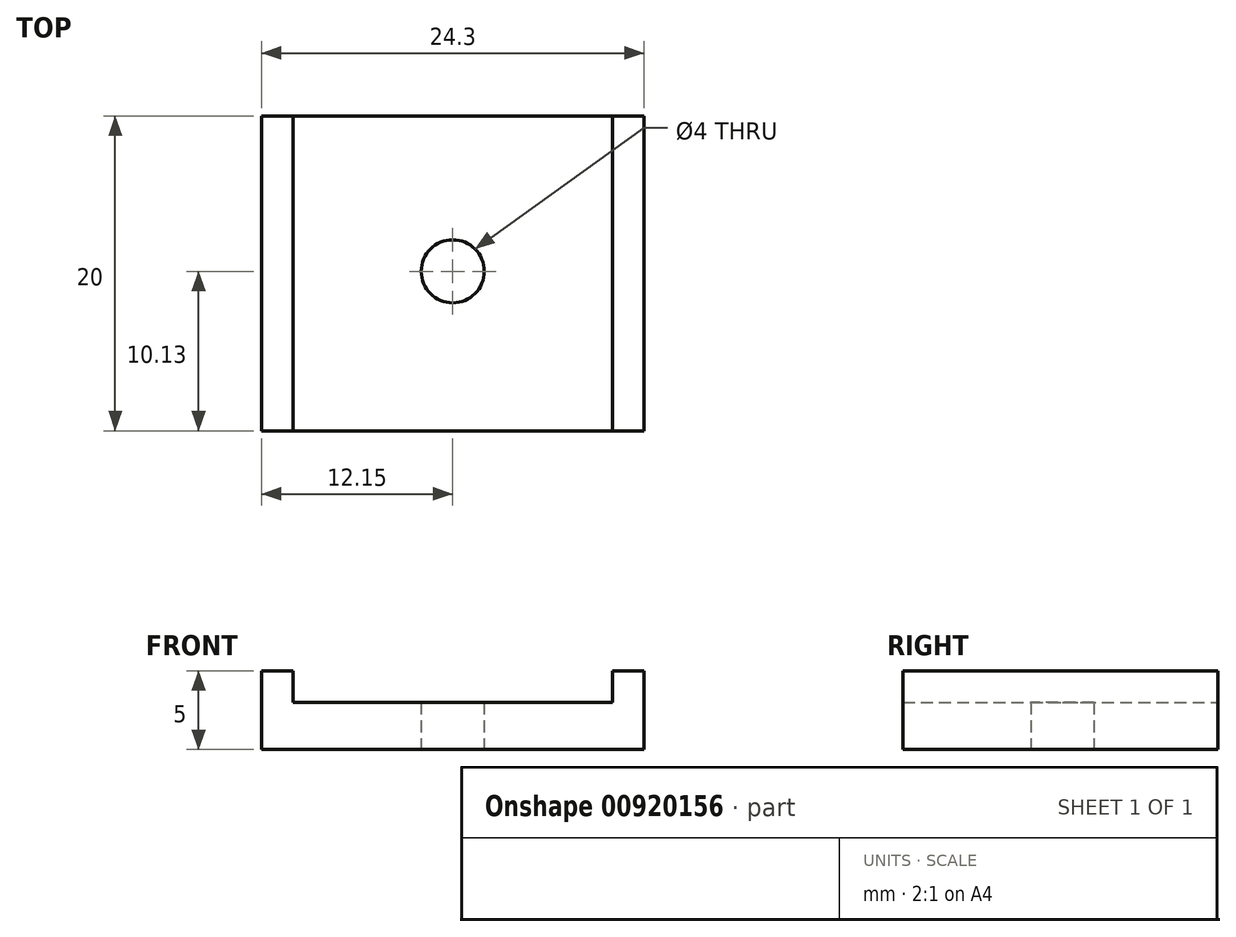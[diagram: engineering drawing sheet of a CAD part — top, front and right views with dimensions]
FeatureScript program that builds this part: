
annotation { "Feature Type Name" : "Feature", "Feature Type Description" : "" }
export const myFeature = defineFeature(function(context is Context, id is Id, definition is map)
    precondition{}
    {
        {
            var Q0;
            Q0=qCreatedBy(makeId("Top.planeOp"),FACE);
            var sketch = newSketch(context, id + "F0", { "sketchPlane" : qUnion([Q0])});
            skLineSegment(sketch, "E0", {"start": v(0, 0) * mm, "end": v(0, 41.66) * mm, "construction": true});
            skLineSegment(sketch, "E1", {"start": v(0, -0.13) * mm, "end": v(10.15, -0.13) * mm});
            skLineSegment(sketch, "E2", {"start": v(10.15, 19.87) * mm, "end": v(0, 19.87) * mm});
            skLineSegment(sketch, "E3.MirrorCS", {"start": v(-10.15, 19.87) * mm, "end": v(0, 19.87) * mm});
            skLineSegment(sketch, "E4.MirrorCS", {"start": v(0, -0.13) * mm, "end": v(-10.15, -0.13) * mm});
            skCircle(sketch, "E5", {"center": v(0, 10) * mm, "radius": 2 * mm});
            skLineSegment(sketch, "E6.bottom", {"start": v(10.15, -0.13) * mm, "end": v(12.15, -0.13) * mm});
            skLineSegment(sketch, "E6.top", {"start": v(10.15, 19.87) * mm, "end": v(12.15, 19.87) * mm});
            skLineSegment(sketch, "E6.right", {"start": v(12.15, -0.13) * mm, "end": v(12.15, 19.87) * mm});
            skLineSegment(sketch, "E7.MirrorCS", {"start": v(-12.15, -0.13) * mm, "end": v(-12.15, 19.87) * mm});
            skLineSegment(sketch, "E8.MirrorCS", {"start": v(-10.15, 19.87) * mm, "end": v(-12.15, 19.87) * mm});
            skLineSegment(sketch, "E9.MirrorCS", {"start": v(-10.15, -0.13) * mm, "end": v(-12.15, -0.13) * mm});
            skSolve(sketch);
        }
        {
            var Q0;
            Q0=makeQuery(id+"F0.imprint","IMPRINT",FACE,{"disambiguationData":[TD([[makeQuery(id+"F0.imprint","IMPRINT",EDGE,{"derivedFrom":sQuery(id+"F0.wireOp",EDGE,"E1")}),1.0]])]});
            extrude(context, id + "F1", {"entities" : qUnion([Q0]), "depth" : 3 * mm, "offsetDistance" : 25 * mm});
        }
        {
            var Q0;
            Q0=makeQuery(id+"F1.opExtrude","CAP_FACE",FACE,{"disambiguationData":[OSD([sQuery(id+"F0.wireOp",EDGE,"E1"),sQuery(id+"F0.wireOp",EDGE,"E2"),sQuery(id+"F0.wireOp",EDGE,"E3.MirrorCS"),sQuery(id+"F0.wireOp",EDGE,"E4.MirrorCS"),sQuery(id+"F0.wireOp",EDGE,"E5"),sQuery(id+"F0.wireOp",EDGE,"E6.bottom"),sQuery(id+"F0.wireOp",EDGE,"E6.top"),sQuery(id+"F0.wireOp",EDGE,"E6.right"),sQuery(id+"F0.wireOp",EDGE,"E7.MirrorCS"),sQuery(id+"F0.wireOp",EDGE,"E8.MirrorCS"),sQuery(id+"F0.wireOp",EDGE,"E9.MirrorCS")])],"isStart":false});
            var sketch = newSketch(context, id + "F2", { "sketchPlane" : qUnion([Q0])});
            skLineSegment(sketch, "E10.bottom", {"start": v(12.15, -0.13) * mm, "end": v(10.15, -0.13) * mm});
            skLineSegment(sketch, "E10.top", {"start": v(12.15, 19.87) * mm, "end": v(10.15, 19.87) * mm});
            skLineSegment(sketch, "E10.left", {"start": v(12.15, -0.13) * mm, "end": v(12.15, 19.87) * mm});
            skLineSegment(sketch, "E10.right", {"start": v(10.15, -0.13) * mm, "end": v(10.15, 19.87) * mm});
            skLineSegment(sketch, "E11", {"start": v(0, 0) * mm, "end": v(0, 19.87) * mm, "construction": true});
            skLineSegment(sketch, "E12.MirrorCS", {"start": v(-10.15, -0.13) * mm, "end": v(-10.15, 19.87) * mm});
            skLineSegment(sketch, "E13.MirrorCS", {"start": v(-12.15, -0.13) * mm, "end": v(-12.15, 19.87) * mm});
            skLineSegment(sketch, "E14.MirrorCS", {"start": v(-12.15, -0.13) * mm, "end": v(-10.15, -0.13) * mm});
            skLineSegment(sketch, "E15.MirrorCS", {"start": v(-12.15, 19.87) * mm, "end": v(-10.15, 19.87) * mm});
            skSolve(sketch);
        }
        {
            var Q0;
            Q0=makeQuery(id+"F2.imprint","IMPRINT",FACE,{"disambiguationData":[TD([[makeQuery(id+"F2.imprint","IMPRINT",EDGE,{"derivedFrom":sQuery(id+"F2.wireOp",EDGE,"E10.bottom")}),-1.0]])]});
            var Q1;
            Q1=makeQuery(id+"F2.imprint","IMPRINT",FACE,{"disambiguationData":[TD([[makeQuery(id+"F2.imprint","IMPRINT",EDGE,{"derivedFrom":sQuery(id+"F2.wireOp",EDGE,"E12.MirrorCS")}),1.0]])]});
            extrude(context, id + "F3", {"entities" : qUnion([Q0, Q1]), "operationType" : NewBodyOperationType.ADD, "depth" : 2 * mm, "offsetDistance" : 25 * mm});
        }
    });
